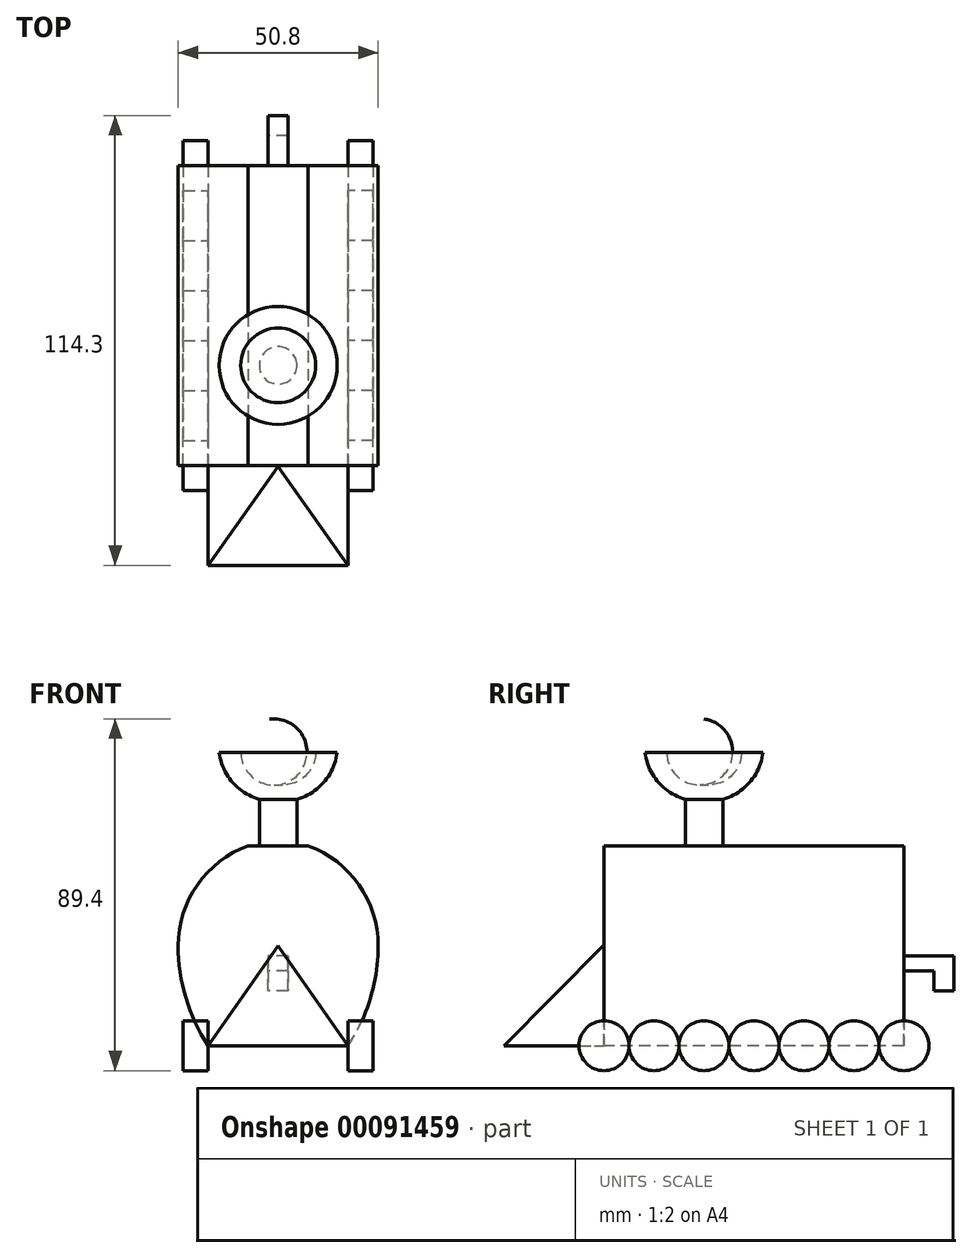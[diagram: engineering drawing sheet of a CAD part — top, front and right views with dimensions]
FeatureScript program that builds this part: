
annotation { "Feature Type Name" : "Feature", "Feature Type Description" : "" }
export const myFeature = defineFeature(function(context is Context, id is Id, definition is map)
    precondition{}
    {
        {
            var Q0;
            Q0=qCreatedBy(makeId("Front.planeOp"),FACE);
            var sketch = newSketch(context, id + "F0", { "sketchPlane" : qUnion([Q0])});
            skLineSegment(sketch, "E0", {"start": v(0, 0) * mm, "end": v(0, 50.8) * mm});
            skLineSegment(sketch, "E1", {"start": v(0, 50.8) * mm, "end": v(50.8, 50.8) * mm});
            skLineSegment(sketch, "E2", {"start": v(50.8, 50.8) * mm, "end": v(50.8, 0) * mm});
            skLineSegment(sketch, "E3", {"start": v(50.8, 0) * mm, "end": v(0, 0) * mm});
            skSolve(sketch);
        }
        {
            var Q0;
            Q0=makeQuery(id+"F0.imprint","IMPRINT",FACE,{"disambiguationData":[TD([[makeQuery(id+"F0.imprint","IMPRINT",EDGE,{"derivedFrom":sQuery(id+"F0.wireOp",EDGE,"E0")}),-1.0]])]});
            extrude(context, id + "F1", {"entities" : qUnion([Q0]), "depth" : 76.2 * mm});
        }
        {
            var Q0;
            Q0=qCreatedBy(makeId("Right.planeOp"),FACE);
            cPlane(context, id + "F2", {"entities" : qUnion([Q0]), "cplaneType" : CPlaneType.OFFSET, "offset" : 50.8 * mm, "width" : 152.4 * mm, "height" : 152.4 * mm});
        }
        {
            var Q0;
            Q0=qCreatedBy(makeId("Front.planeOp"),FACE);
            cPlane(context, id + "F3", {"entities" : qUnion([Q0]), "cplaneType" : CPlaneType.OFFSET, "offset" : 76.2 * mm, "width" : 152.4 * mm, "height" : 152.4 * mm});
        }
        {
            var Q0;
            Q0=qCreatedBy(id+"F3.planeOp",FACE);
            var sketch = newSketch(context, id + "F4", { "sketchPlane" : qUnion([Q0])});
            skLineSegment(sketch, "E4", {"start": v(0, 0) * mm, "end": v(0, 50.8) * mm});
            skLineSegment(sketch, "E5", {"start": v(0, 50.8) * mm, "end": v(50.8, 50.8) * mm});
            skLineSegment(sketch, "E6", {"start": v(50.8, 50.8) * mm, "end": v(50.8, 0) * mm});
            skLineSegment(sketch, "E7", {"start": v(50.8, 0) * mm, "end": v(0, 0) * mm});
            skLineSegment(sketch, "E8", {"start": v(43.18, 0) * mm, "end": v(25.4, 25.4) * mm});
            skPoint(sketch, "E8.endSnap0", {"position": v(25.4, 50.8) * mm});
            skPoint(sketch, "E8.endSnap1", {"position": v(0, 25.4) * mm});
            skLineSegment(sketch, "E9", {"start": v(25.4, 25.4) * mm, "end": v(7.62, 0) * mm});
            skSolve(sketch);
        }
        {
            var Q0;
            {var subQ0=sQuery(id+"F4.wireOp",EDGE,"E8");Q0=makeQuery(id+"F4.imprint","IMPRINT",FACE,{"disambiguationData":[TD([[makeQuery(id+"F4.imprint","IMPRINT",EDGE,{"derivedFrom":subQ0}),1.0]])]});}
            extrude(context, id + "F5", {"entities" : qUnion([Q0]), "operationType" : NewBodyOperationType.ADD, "depth" : 25.4 * mm});
        }
        {
            var Q0;
            Q0=qCreatedBy(makeId("Right.planeOp"),FACE);
            var sketch = newSketch(context, id + "F6", { "sketchPlane" : qUnion([Q0])});
            skLineSegment(sketch, "E10", {"start": v(-101.6, 0) * mm, "end": v(-76.53, 25.4) * mm});
            skLineSegment(sketch, "E11", {"start": v(-76.53, 25.4) * mm, "end": v(-101.93, 25.4) * mm});
            skLineSegment(sketch, "E12", {"start": v(-101.93, 25.4) * mm, "end": v(-101.6, 0) * mm});
            skSolve(sketch);
        }
        {
            var Q0;
            Q0=makeQuery(id+"F6.imprint","IMPRINT",FACE,{"disambiguationData":[TD([[makeQuery(id+"F6.imprint","IMPRINT",EDGE,{"derivedFrom":sQuery(id+"F6.wireOp",EDGE,"E10")}),1.0]])]});
            extrude(context, id + "F7", {"entities" : qUnion([Q0]), "operationType" : NewBodyOperationType.REMOVE, "depth" : 50.8 * mm});
        }
        {
            var Q0;
            Q0=qCreatedBy(makeId("Right.planeOp"),FACE);
            cPlane(context, id + "F8", {"entities" : qUnion([Q0]), "cplaneType" : CPlaneType.OFFSET, "offset" : 25.4 * mm, "width" : 152.4 * mm, "height" : 152.4 * mm});
        }
        {
            var Q0;
            Q0=qCreatedBy(id+"F8.planeOp",FACE);
            var sketch = newSketch(context, id + "F9", { "sketchPlane" : qUnion([Q0])});
            skLineSegment(sketch, "E13", {"start": v(-50.8, 50.8) * mm, "end": v(-50.8, 66.3) * mm});
            skArc(sketch, "E14", {"start": v(-60.3, 74.53) * mm, "mid": v(-57.4, 68.28) * mm, "end": v(-50.8, 66.3) * mm});
            skLineSegment(sketch, "E15", {"start": v(-60.3, 74.53) * mm, "end": v(-65.8, 74.53) * mm});
            skArc(sketch, "E16", {"start": v(-65.8, 74.53) * mm, "mid": v(-62.47, 67.01) * mm, "end": v(-55.57, 62.56) * mm});
            skLineSegment(sketch, "E17", {"start": v(-50.8, 50.8) * mm, "end": v(-55.57, 50.8) * mm});
            skLineSegment(sketch, "E18", {"start": v(-55.57, 50.8) * mm, "end": v(-55.57, 62.56) * mm});
            skSolve(sketch);
        }
        {
            var Q0;
            Q0 = qSketchRegion(id + "F9", true);
            var Q1;
            Q1=sQuery(id+"F9.wireOp",EDGE,"E13");
            revolve(context, id + "F10", {"operationType" : NewBodyOperationType.ADD, "entities" : qUnion([Q0]), "axis" : qUnion([Q1]), "revolveType" : RevolveType.FULL});
        }
        {
            var Q0;
            Q0=makeQuery(id+"F1.opExtrude","CAP_FACE",FACE,{"disambiguationData":[OSD([sQuery(id+"F0.wireOp",EDGE,"E0"),sQuery(id+"F0.wireOp",EDGE,"E1"),sQuery(id+"F0.wireOp",EDGE,"E2"),sQuery(id+"F0.wireOp",EDGE,"E3")])],"isStart":false});
            var sketch = newSketch(context, id + "F11", { "sketchPlane" : qUnion([Q0])});
            skArc(sketch, "E19", {"start": v(17.78, 50.8) * mm, "mid": v(4.89, 40.9) * mm, "end": v(0, 25.4) * mm});
            skArc(sketch, "E20", {"start": v(50.8, 25.4) * mm, "mid": v(45.91, 40.9) * mm, "end": v(33.02, 50.8) * mm});
            skLineSegment(sketch, "E21", {"start": v(0, 25.4) * mm, "end": v(0, 50.8) * mm});
            skLineSegment(sketch, "E22", {"start": v(0, 50.8) * mm, "end": v(17.78, 50.8) * mm});
            skLineSegment(sketch, "E23", {"start": v(33.02, 50.8) * mm, "end": v(50.8, 50.8) * mm});
            skLineSegment(sketch, "E24", {"start": v(50.8, 50.8) * mm, "end": v(50.8, 25.4) * mm});
            skArc(sketch, "E25", {"start": v(0, 25.4) * mm, "mid": v(1.95, 12.14) * mm, "end": v(7.62, 0) * mm});
            skArc(sketch, "E26", {"start": v(43.18, 0) * mm, "mid": v(48.85, 12.14) * mm, "end": v(50.8, 25.4) * mm});
            skLineSegment(sketch, "E27", {"start": v(0, 25.4) * mm, "end": v(0, 0) * mm});
            skLineSegment(sketch, "E28", {"start": v(0, 0) * mm, "end": v(7.62, 0) * mm});
            skLineSegment(sketch, "E29", {"start": v(43.18, 0) * mm, "end": v(50.8, 0) * mm});
            skLineSegment(sketch, "E30", {"start": v(50.8, 0) * mm, "end": v(50.8, 25.4) * mm});
            skSolve(sketch);
        }
        {
            var Q0;
            Q0=makeQuery(id+"F11.imprint","IMPRINT",FACE,{"disambiguationData":[TD([[makeQuery(id+"F11.imprint","IMPRINT",EDGE,{"derivedFrom":sQuery(id+"F11.wireOp",EDGE,"E20")}),-1.0]])]});
            var Q1;
            Q1=makeQuery(id+"F11.imprint","IMPRINT",FACE,{"disambiguationData":[TD([[makeQuery(id+"F11.imprint","IMPRINT",EDGE,{"derivedFrom":sQuery(id+"F11.wireOp",EDGE,"E19")}),-1.0]])]});
            var Q2;
            Q2=makeQuery(id+"F11.imprint","IMPRINT",FACE,{"disambiguationData":[TD([[makeQuery(id+"F11.imprint","IMPRINT",EDGE,{"derivedFrom":sQuery(id+"F11.wireOp",EDGE,"E25")}),-1.0]])]});
            var Q3;
            Q3=makeQuery(id+"F11.imprint","IMPRINT",FACE,{"disambiguationData":[TD([[makeQuery(id+"F11.imprint","IMPRINT",EDGE,{"derivedFrom":sQuery(id+"F11.wireOp",EDGE,"E26")}),-1.0]])]});
            extrude(context, id + "F12", {"entities" : qUnion([Q0, Q1, Q2, Q3]), "operationType" : NewBodyOperationType.REMOVE, "oppositeDirection" : true, "depth" : 76.2 * mm});
        }
        {
            var Q0;
            Q0=qCreatedBy(makeId("Right.planeOp"),FACE);
            cPlane(context, id + "F13", {"entities" : qUnion([Q0]), "cplaneType" : CPlaneType.OFFSET, "offset" : 7.62 * mm, "width" : 152.4 * mm, "height" : 152.4 * mm});
        }
        {
            var Q0;
            Q0=qCreatedBy(id+"F13.planeOp",FACE);
            var sketch = newSketch(context, id + "F14", { "sketchPlane" : qUnion([Q0])});
            skCircle(sketch, "E31", {"center": v(-12.7, 0) * mm, "radius": 6.35 * mm});
            skCircle(sketch, "E32", {"center": v(-25.4, 0) * mm, "radius": 6.35 * mm});
            skCircle(sketch, "E33", {"center": v(-38.1, 0) * mm, "radius": 6.35 * mm});
            skCircle(sketch, "E34", {"center": v(-50.8, 0) * mm, "radius": 6.35 * mm});
            skCircle(sketch, "E35", {"center": v(-63.5, 0) * mm, "radius": 6.35 * mm});
            skCircle(sketch, "E36", {"center": v(0, 0) * mm, "radius": 6.35 * mm});
            skCircle(sketch, "E37", {"center": v(-76.2, 0) * mm, "radius": 6.35 * mm});
            skSolve(sketch);
        }
        {
            var Q0;
            Q0 = qSketchRegion(id + "F14", true);
            extrude(context, id + "F15", {"entities" : qUnion([Q0]), "oppositeDirection" : true, "depth" : 6.35 * mm});
        }
        {
            var Q0;
            Q0=qCreatedBy(id+"F2.planeOp",FACE);
            cPlane(context, id + "F16", {"entities" : qUnion([Q0]), "cplaneType" : CPlaneType.OFFSET, "offset" : 7.62 * mm, "oppositeDirection" : true, "width" : 152.4 * mm, "height" : 152.4 * mm});
        }
        {
            var Q0;
            Q0=qCreatedBy(id+"F16.planeOp",FACE);
            var sketch = newSketch(context, id + "F17", { "sketchPlane" : qUnion([Q0])});
            skCircle(sketch, "E38", {"center": v(-76.2, 0) * mm, "radius": 6.35 * mm});
            skCircle(sketch, "E39", {"center": v(-63.5, 0) * mm, "radius": 6.35 * mm});
            skCircle(sketch, "E40", {"center": v(-50.8, 0) * mm, "radius": 6.35 * mm});
            skCircle(sketch, "E41", {"center": v(-38.1, 0) * mm, "radius": 6.35 * mm});
            skCircle(sketch, "E42", {"center": v(-25.4, 0) * mm, "radius": 6.35 * mm});
            skCircle(sketch, "E43", {"center": v(-12.7, 0) * mm, "radius": 6.35 * mm});
            skCircle(sketch, "E44", {"center": v(0, 0) * mm, "radius": 6.35 * mm});
            skSolve(sketch);
        }
        {
            var Q0;
            Q0 = qSketchRegion(id + "F17", true);
            extrude(context, id + "F18", {"entities" : qUnion([Q0]), "depth" : 6.35 * mm});
        }
        {
            var Q0;
            Q0=qCreatedBy(id+"F8.planeOp",FACE);
            var sketch = newSketch(context, id + "F19", { "sketchPlane" : qUnion([Q0])});
            skLineSegment(sketch, "E45", {"start": v(0, 19.05) * mm, "end": v(7.62, 19.05) * mm});
            skLineSegment(sketch, "E46", {"start": v(7.62, 19.05) * mm, "end": v(7.62, 13.97) * mm});
            skLineSegment(sketch, "E47", {"start": v(7.62, 13.97) * mm, "end": v(12.7, 13.97) * mm});
            skLineSegment(sketch, "E48", {"start": v(12.7, 13.97) * mm, "end": v(12.7, 22.86) * mm});
            skLineSegment(sketch, "E49", {"start": v(12.7, 22.86) * mm, "end": v(0, 22.86) * mm});
            skLineSegment(sketch, "E50", {"start": v(0, 22.86) * mm, "end": v(0, 19.05) * mm});
            skSolve(sketch);
        }
        {
            var Q0;
            Q0=makeQuery(id+"F19.imprint","IMPRINT",FACE,{"disambiguationData":[TD([[makeQuery(id+"F19.imprint","IMPRINT",EDGE,{"derivedFrom":sQuery(id+"F19.wireOp",EDGE,"E45")}),1.0]])]});
            extrude(context, id + "F20", {"entities" : qUnion([Q0]), "operationType" : NewBodyOperationType.ADD, "depth" : 2.54 * mm});
        }
        {
            var Q0;
            Q0 = qSketchRegion(id + "F19", true);
            extrude(context, id + "F21", {"entities" : qUnion([Q0]), "operationType" : NewBodyOperationType.ADD, "oppositeDirection" : true, "depth" : 2.54 * mm});
        }
    });
